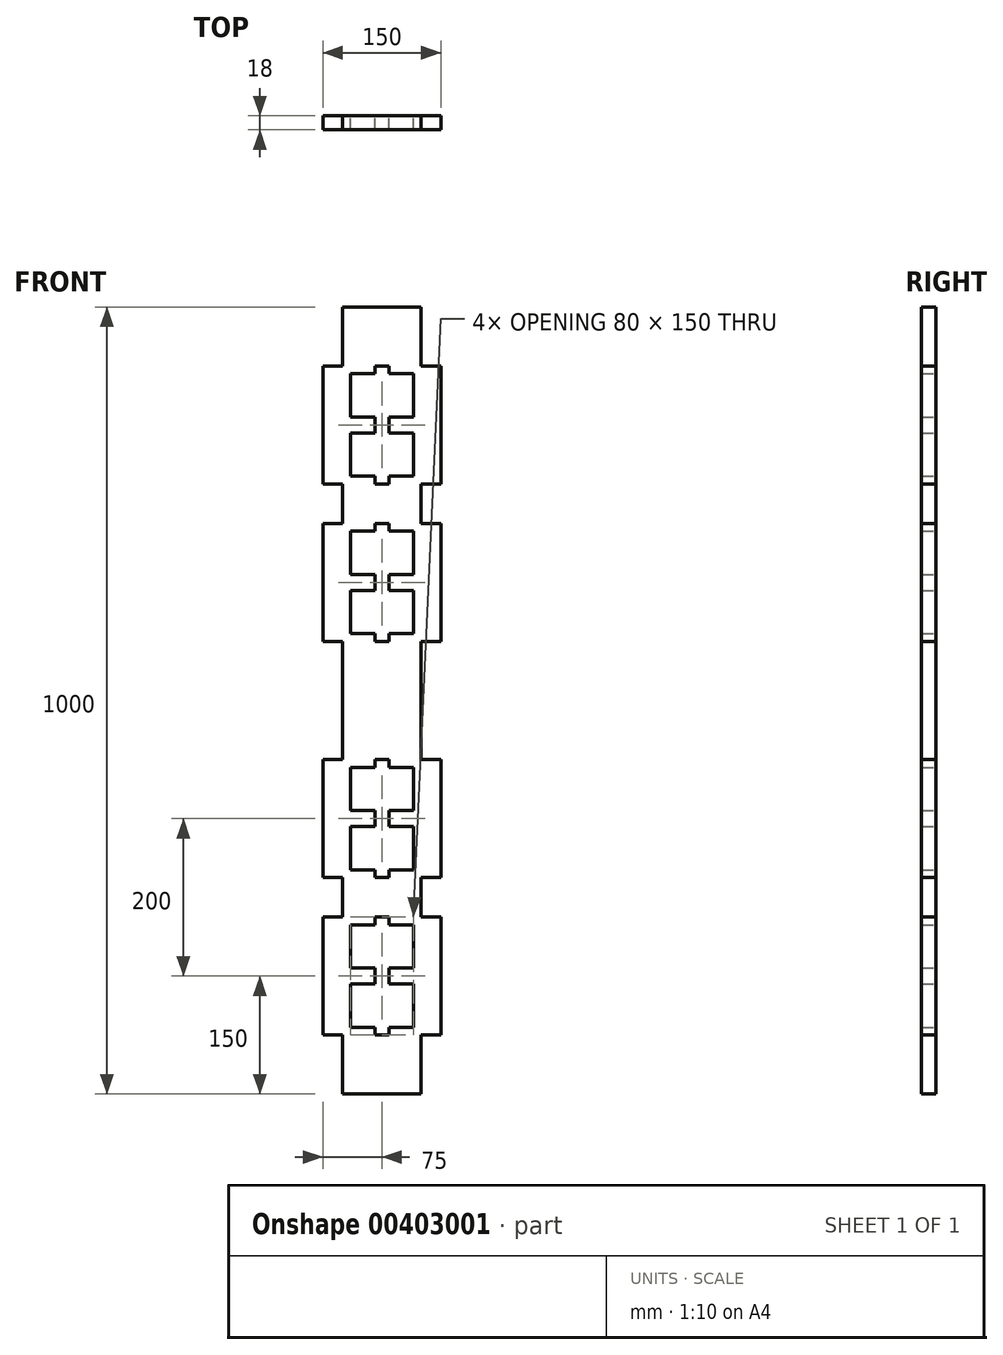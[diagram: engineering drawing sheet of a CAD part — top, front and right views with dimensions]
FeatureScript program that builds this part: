
annotation { "Feature Type Name" : "Feature", "Feature Type Description" : "" }
export const myFeature = defineFeature(function(context is Context, id is Id, definition is map)
    precondition{}
    {
        {
            var Q0;
            Q0=qCreatedBy(makeId("Front.planeOp"),FACE);
            var sketch = newSketch(context, id + "F0", { "sketchPlane" : qUnion([Q0])});
            skLineSegment(sketch, "E0.bottom", {"start": v(-50, 0) * mm, "end": v(50, 0) * mm});
            skLineSegment(sketch, "E0.top", {"start": v(-50, 1000) * mm, "end": v(50, 1000) * mm});
            skLineSegment(sketch, "E0.right", {"start": v(50, 0) * mm, "end": v(50, 75) * mm});
            skLineSegment(sketch, "E1.bottom", {"start": v(50, 925) * mm, "end": v(75, 925) * mm});
            skLineSegment(sketch, "E1.top", {"start": v(50, 775) * mm, "end": v(75, 775) * mm});
            skLineSegment(sketch, "E1.right", {"start": v(75, 925) * mm, "end": v(75, 775) * mm});
            skLineSegment(sketch, "E2.bottom", {"start": v(50, 425) * mm, "end": v(75, 425) * mm});
            skLineSegment(sketch, "E2.top", {"start": v(50, 275) * mm, "end": v(75, 275) * mm});
            skLineSegment(sketch, "E2.right", {"start": v(75, 425) * mm, "end": v(75, 275) * mm});
            skLineSegment(sketch, "E3.trimOffspring", {"start": v(50, 925) * mm, "end": v(50, 1000) * mm});
            skLineSegment(sketch, "E4.trimOffspring", {"start": v(50, 425) * mm, "end": v(50, 575) * mm});
            skLineSegment(sketch, "E5.bottom", {"start": v(75, 725) * mm, "end": v(50, 725) * mm});
            skLineSegment(sketch, "E5.top", {"start": v(75, 575) * mm, "end": v(50, 575) * mm});
            skLineSegment(sketch, "E5.right", {"start": v(75, 725) * mm, "end": v(75, 575) * mm});
            skLineSegment(sketch, "E6.bottom", {"start": v(75, 225) * mm, "end": v(50, 225) * mm});
            skLineSegment(sketch, "E6.top", {"start": v(75, 75) * mm, "end": v(50, 75) * mm});
            skLineSegment(sketch, "E6.right", {"start": v(75, 225) * mm, "end": v(75, 75) * mm});
            skLineSegment(sketch, "E7.trimOffspring", {"start": v(50, 725) * mm, "end": v(50, 775) * mm});
            skLineSegment(sketch, "E8.trimOffspring", {"start": v(50, 225) * mm, "end": v(50, 275) * mm});
            skLineSegment(sketch, "E9.bottom", {"start": v(-50, 925) * mm, "end": v(-75, 925) * mm});
            skLineSegment(sketch, "E9.top", {"start": v(-50, 775) * mm, "end": v(-75, 775) * mm});
            skLineSegment(sketch, "E9.right", {"start": v(-75, 925) * mm, "end": v(-75, 775) * mm});
            skLineSegment(sketch, "E10.bottom", {"start": v(-50, 725) * mm, "end": v(-75, 725) * mm});
            skLineSegment(sketch, "E10.top", {"start": v(-50, 575) * mm, "end": v(-75, 575) * mm});
            skLineSegment(sketch, "E10.right", {"start": v(-75, 725) * mm, "end": v(-75, 575) * mm});
            skLineSegment(sketch, "E11.bottom", {"start": v(-50, 425) * mm, "end": v(-75, 425) * mm});
            skLineSegment(sketch, "E11.top", {"start": v(-50, 275) * mm, "end": v(-75, 275) * mm});
            skLineSegment(sketch, "E11.right", {"start": v(-75, 425) * mm, "end": v(-75, 275) * mm});
            skLineSegment(sketch, "E12.bottom", {"start": v(-50, 225) * mm, "end": v(-75, 225) * mm});
            skLineSegment(sketch, "E12.top", {"start": v(-50, 75) * mm, "end": v(-75, 75) * mm});
            skLineSegment(sketch, "E12.right", {"start": v(-75, 225) * mm, "end": v(-75, 75) * mm});
            skLineSegment(sketch, "E13", {"start": v(-50, 1000) * mm, "end": v(-50, 925) * mm});
            skPoint(sketch, "E14.orphan", {"position": v(0, 0) * mm});
            skLineSegment(sketch, "E15.trimOffspring", {"start": v(-50, 775) * mm, "end": v(-50, 725) * mm});
            skLineSegment(sketch, "E16.trimOffspring", {"start": v(-50, 575) * mm, "end": v(-50, 425) * mm});
            skLineSegment(sketch, "E17.trimOffspring", {"start": v(-50, 275) * mm, "end": v(-50, 225) * mm});
            skLineSegment(sketch, "E18.trimOffspring", {"start": v(-50, 75) * mm, "end": v(-50, 0) * mm});
            skLineSegment(sketch, "E19.bottom", {"start": v(-9, 925) * mm, "end": v(9, 925) * mm});
            skLineSegment(sketch, "E19.top", {"start": v(-9, 775) * mm, "end": v(9, 775) * mm});
            skLineSegment(sketch, "E19.left", {"start": v(-9, 925) * mm, "end": v(-9, 915) * mm});
            skLineSegment(sketch, "E19.right", {"start": v(9, 925) * mm, "end": v(9, 915) * mm});
            skLineSegment(sketch, "E20.bottom", {"start": v(-9, 725) * mm, "end": v(9, 725) * mm});
            skLineSegment(sketch, "E20.top", {"start": v(-9, 575) * mm, "end": v(9, 575) * mm});
            skLineSegment(sketch, "E20.left", {"start": v(-9, 725) * mm, "end": v(-9, 715) * mm});
            skLineSegment(sketch, "E20.right", {"start": v(9, 725) * mm, "end": v(9, 715) * mm});
            skLineSegment(sketch, "E21.bottom", {"start": v(-9, 425) * mm, "end": v(9, 425) * mm});
            skLineSegment(sketch, "E21.top", {"start": v(-9, 275) * mm, "end": v(9, 275) * mm});
            skLineSegment(sketch, "E21.left", {"start": v(-9, 425) * mm, "end": v(-9, 415) * mm});
            skLineSegment(sketch, "E21.right", {"start": v(9, 425) * mm, "end": v(9, 415) * mm});
            skLineSegment(sketch, "E22.bottom", {"start": v(-9, 225) * mm, "end": v(9, 225) * mm});
            skLineSegment(sketch, "E22.top", {"start": v(-9, 75) * mm, "end": v(9, 75) * mm});
            skLineSegment(sketch, "E22.left", {"start": v(-9, 225) * mm, "end": v(-9, 215) * mm});
            skLineSegment(sketch, "E22.right", {"start": v(9, 225) * mm, "end": v(9, 215) * mm});
            skLineSegment(sketch, "E23.bottom", {"start": v(-40, 915) * mm, "end": v(-9, 915) * mm});
            skLineSegment(sketch, "E23.top", {"start": v(-40, 860) * mm, "end": v(-9, 860) * mm});
            skLineSegment(sketch, "E23.left", {"start": v(-40, 915) * mm, "end": v(-40, 860) * mm});
            skLineSegment(sketch, "E23.right", {"start": v(40, 915) * mm, "end": v(40, 860) * mm});
            skLineSegment(sketch, "E24.bottom", {"start": v(-40, 840) * mm, "end": v(-9, 840) * mm});
            skLineSegment(sketch, "E24.top", {"start": v(-40, 785) * mm, "end": v(-9, 785) * mm});
            skLineSegment(sketch, "E24.left", {"start": v(-40, 840) * mm, "end": v(-40, 785) * mm});
            skLineSegment(sketch, "E24.right", {"start": v(40, 840) * mm, "end": v(40, 785) * mm});
            skLineSegment(sketch, "E25.bottom", {"start": v(-40, 715) * mm, "end": v(-9, 715) * mm});
            skLineSegment(sketch, "E25.top", {"start": v(-40, 660) * mm, "end": v(-9, 660) * mm});
            skLineSegment(sketch, "E25.left", {"start": v(-40, 715) * mm, "end": v(-40, 660) * mm});
            skLineSegment(sketch, "E25.right", {"start": v(40, 715) * mm, "end": v(40, 660) * mm});
            skLineSegment(sketch, "E26.bottom", {"start": v(-40, 640) * mm, "end": v(-9, 640) * mm});
            skLineSegment(sketch, "E26.top", {"start": v(-40, 585) * mm, "end": v(-9, 585) * mm});
            skLineSegment(sketch, "E26.left", {"start": v(-40, 640) * mm, "end": v(-40, 585) * mm});
            skLineSegment(sketch, "E26.right", {"start": v(40, 640) * mm, "end": v(40, 585) * mm});
            skLineSegment(sketch, "E27.bottom", {"start": v(-40, 415) * mm, "end": v(-9, 415) * mm});
            skLineSegment(sketch, "E27.top", {"start": v(-40, 360) * mm, "end": v(-9, 360) * mm});
            skLineSegment(sketch, "E27.left", {"start": v(-40, 415) * mm, "end": v(-40, 360) * mm});
            skLineSegment(sketch, "E27.right", {"start": v(40, 415) * mm, "end": v(40, 360) * mm});
            skLineSegment(sketch, "E28.bottom", {"start": v(-40, 340) * mm, "end": v(-9, 340) * mm});
            skLineSegment(sketch, "E28.top", {"start": v(-40, 285) * mm, "end": v(-9, 285) * mm});
            skLineSegment(sketch, "E28.left", {"start": v(-40, 340) * mm, "end": v(-40, 285) * mm});
            skLineSegment(sketch, "E28.right", {"start": v(40, 340) * mm, "end": v(40, 285) * mm});
            skLineSegment(sketch, "E29.bottom", {"start": v(-40, 215) * mm, "end": v(-9, 215) * mm});
            skLineSegment(sketch, "E29.top", {"start": v(-40, 160) * mm, "end": v(-9, 160) * mm});
            skLineSegment(sketch, "E29.left", {"start": v(-40, 215) * mm, "end": v(-40, 160) * mm});
            skLineSegment(sketch, "E29.right", {"start": v(40, 215) * mm, "end": v(40, 160) * mm});
            skLineSegment(sketch, "E30.bottom", {"start": v(-40, 140) * mm, "end": v(-9, 140) * mm});
            skLineSegment(sketch, "E30.top", {"start": v(-40, 85) * mm, "end": v(-9, 85) * mm});
            skLineSegment(sketch, "E30.left", {"start": v(-40, 140) * mm, "end": v(-40, 85) * mm});
            skLineSegment(sketch, "E30.right", {"start": v(40, 140) * mm, "end": v(40, 85) * mm});
            skLineSegment(sketch, "E31.trimOffspring", {"start": v(9, 915) * mm, "end": v(40, 915) * mm});
            skLineSegment(sketch, "E32.trimOffspring", {"start": v(-9, 860) * mm, "end": v(-9, 840) * mm});
            skLineSegment(sketch, "E33.trimOffspring", {"start": v(9, 860) * mm, "end": v(9, 840) * mm});
            skLineSegment(sketch, "E34.trimOffspring", {"start": v(9, 860) * mm, "end": v(40, 860) * mm});
            skLineSegment(sketch, "E35.trimOffspring", {"start": v(9, 840) * mm, "end": v(40, 840) * mm});
            skLineSegment(sketch, "E36.trimOffspring", {"start": v(-9, 785) * mm, "end": v(-9, 775) * mm});
            skLineSegment(sketch, "E37.trimOffspring", {"start": v(9, 785) * mm, "end": v(9, 775) * mm});
            skLineSegment(sketch, "E38.trimOffspring", {"start": v(9, 785) * mm, "end": v(40, 785) * mm});
            skLineSegment(sketch, "E39.trimOffspring", {"start": v(9, 715) * mm, "end": v(40, 715) * mm});
            skLineSegment(sketch, "E40.trimOffspring", {"start": v(-9, 660) * mm, "end": v(-9, 640) * mm});
            skLineSegment(sketch, "E41.trimOffspring", {"start": v(9, 660) * mm, "end": v(9, 640) * mm});
            skLineSegment(sketch, "E42.trimOffspring", {"start": v(9, 660) * mm, "end": v(40, 660) * mm});
            skLineSegment(sketch, "E43.trimOffspring", {"start": v(9, 640) * mm, "end": v(40, 640) * mm});
            skLineSegment(sketch, "E44.trimOffspring", {"start": v(-9, 585) * mm, "end": v(-9, 575) * mm});
            skLineSegment(sketch, "E45.trimOffspring", {"start": v(9, 585) * mm, "end": v(40, 585) * mm});
            skLineSegment(sketch, "E46.trimOffspring", {"start": v(9, 585) * mm, "end": v(9, 575) * mm});
            skLineSegment(sketch, "E47.trimOffspring", {"start": v(9, 415) * mm, "end": v(40, 415) * mm});
            skLineSegment(sketch, "E48.trimOffspring", {"start": v(-9, 360) * mm, "end": v(-9, 340) * mm});
            skLineSegment(sketch, "E49.trimOffspring", {"start": v(9, 360) * mm, "end": v(9, 340) * mm});
            skLineSegment(sketch, "E50.trimOffspring", {"start": v(9, 360) * mm, "end": v(40, 360) * mm});
            skLineSegment(sketch, "E51.trimOffspring", {"start": v(9, 340) * mm, "end": v(40, 340) * mm});
            skLineSegment(sketch, "E52.trimOffspring", {"start": v(-9, 285) * mm, "end": v(-9, 275) * mm});
            skLineSegment(sketch, "E53.trimOffspring", {"start": v(9, 285) * mm, "end": v(40, 285) * mm});
            skLineSegment(sketch, "E54.trimOffspring", {"start": v(9, 285) * mm, "end": v(9, 275) * mm});
            skLineSegment(sketch, "E55.trimOffspring", {"start": v(9, 215) * mm, "end": v(40, 215) * mm});
            skLineSegment(sketch, "E56.trimOffspring", {"start": v(-9, 160) * mm, "end": v(-9, 140) * mm});
            skLineSegment(sketch, "E57.trimOffspring", {"start": v(9, 160) * mm, "end": v(9, 140) * mm});
            skLineSegment(sketch, "E58.trimOffspring", {"start": v(9, 160) * mm, "end": v(40, 160) * mm});
            skLineSegment(sketch, "E59.trimOffspring", {"start": v(9, 140) * mm, "end": v(40, 140) * mm});
            skLineSegment(sketch, "E60.trimOffspring", {"start": v(-9, 85) * mm, "end": v(-9, 75) * mm});
            skLineSegment(sketch, "E61.trimOffspring", {"start": v(9, 85) * mm, "end": v(9, 75) * mm});
            skLineSegment(sketch, "E62.trimOffspring", {"start": v(9, 85) * mm, "end": v(40, 85) * mm});
            skSolve(sketch);
        }
        {
            var Q0;
            Q0=makeQuery(id+"F0.imprint","IMPRINT",FACE,{"disambiguationData":[TD([[makeQuery(id+"F0.imprint","IMPRINT",EDGE,{"derivedFrom":sQuery(id+"F0.wireOp",EDGE,"E0.bottom")}),1.0]])]});
            extrude(context, id + "F1", {"entities" : qUnion([Q0]), "depth" : 18 * mm});
        }
    });
